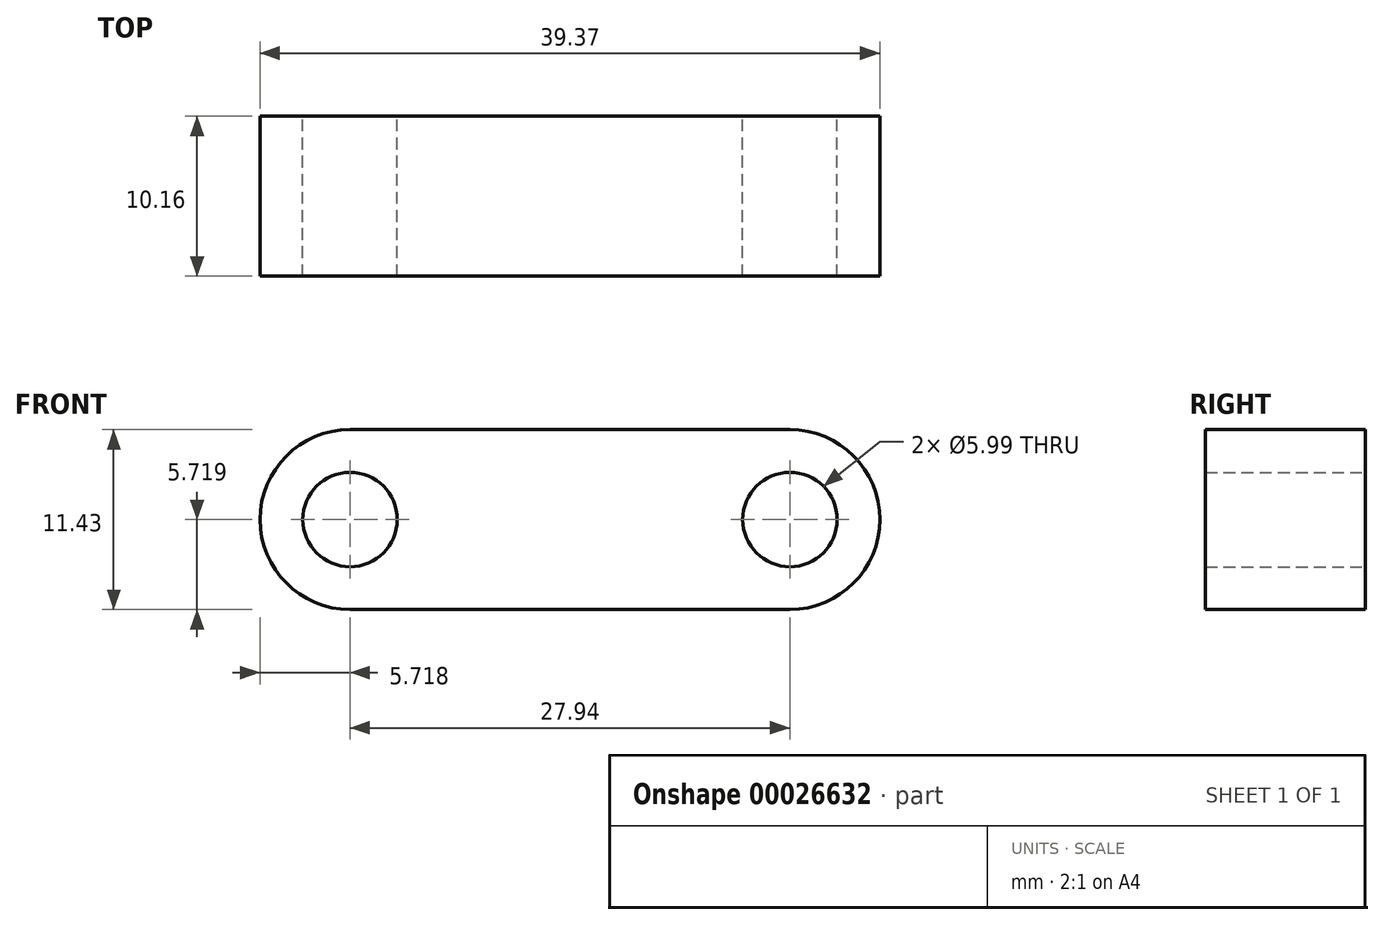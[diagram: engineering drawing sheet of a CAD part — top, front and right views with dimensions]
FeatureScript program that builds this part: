
annotation { "Feature Type Name" : "Feature", "Feature Type Description" : "" }
export const myFeature = defineFeature(function(context is Context, id is Id, definition is map)
    precondition{}
    {
        {
            var Q0;
            Q0=qCreatedBy(makeId("Front.planeOp"),FACE);
            var sketch = newSketch(context, id + "F0", { "sketchPlane" : qUnion([Q0])});
            skLineSegment(sketch, "E0.bottom", {"start": v(-14.72, 0.7) * mm, "end": v(13.22, 0.7) * mm});
            skLineSegment(sketch, "E0.top", {"start": v(-14.72, -10.74) * mm, "end": v(13.22, -10.74) * mm});
            skArc(sketch, "E1", {"start": v(13.22, -10.74) * mm, "mid": v(18.93, -5.02) * mm, "end": v(13.22, 0.7) * mm});
            skArc(sketch, "E2", {"start": v(-14.72, 0.7) * mm, "mid": v(-20.44, -5.02) * mm, "end": v(-14.72, -10.74) * mm});
            skCircle(sketch, "E3", {"center": v(-14.72, -5.02) * mm, "radius": 3 * mm});
            skCircle(sketch, "E4", {"center": v(13.22, -5.02) * mm, "radius": 3 * mm});
            skSolve(sketch);
        }
        {
            var Q0;
            Q0=makeQuery(id+"F0.imprint","IMPRINT",FACE,{"disambiguationData":[TD([[makeQuery(id+"F0.imprint","IMPRINT",EDGE,{"derivedFrom":sQuery(id+"F0.wireOp",EDGE,"E0.bottom")}),-1.0]])]});
            extrude(context, id + "F1", {"entities" : qUnion([Q0]), "depth" : 10.16 * mm});
        }
    });
